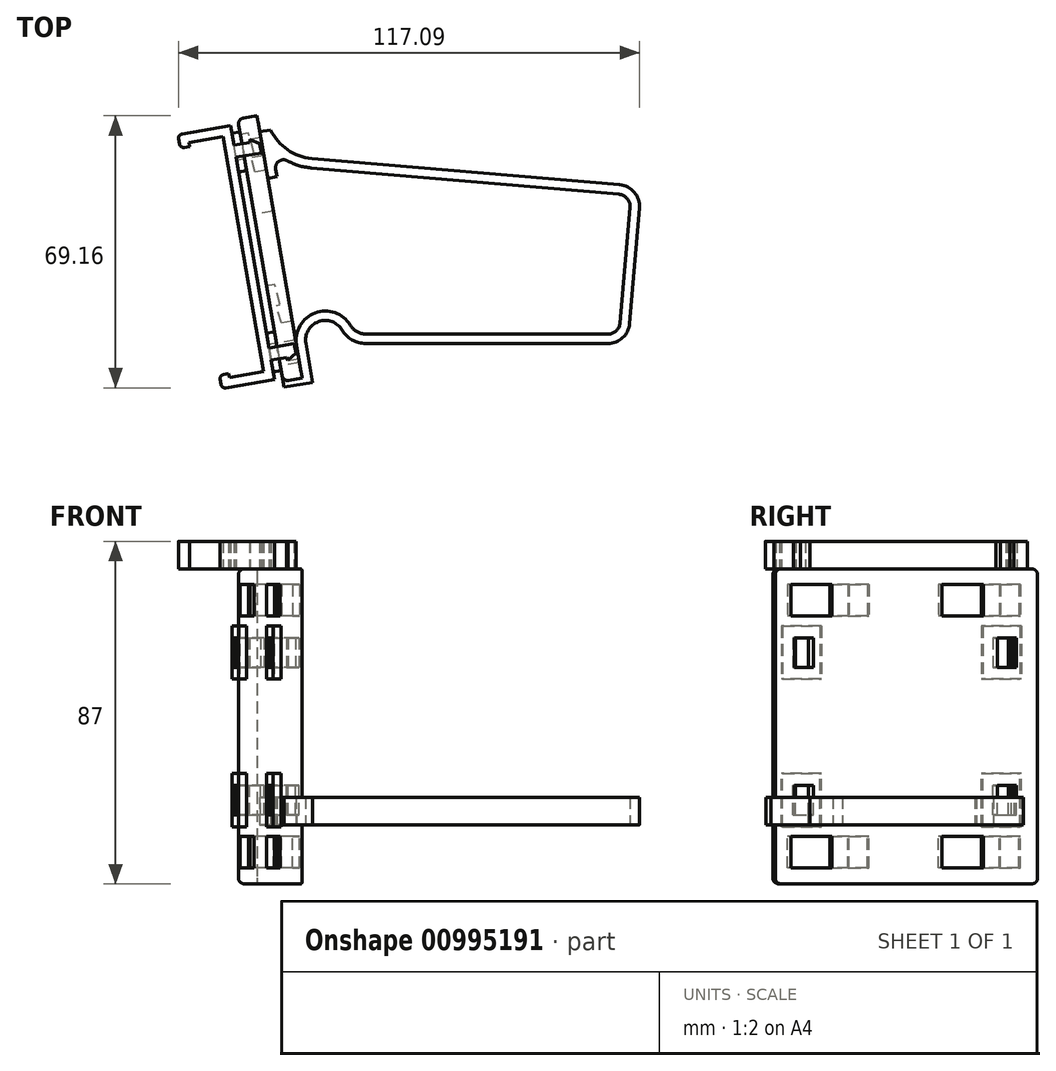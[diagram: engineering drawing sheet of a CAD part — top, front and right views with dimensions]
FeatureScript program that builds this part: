
annotation { "Feature Type Name" : "Feature", "Feature Type Description" : "" }
export const myFeature = defineFeature(function(context is Context, id is Id, definition is map)
    precondition{}
    {
        {
            var Q0;
            Q0=qCreatedBy(makeId("Top.planeOp"),FACE);
            var sketch = newSketch(context, id + "F0", { "sketchPlane" : qUnion([Q0])});
            skLineSegment(sketch, "E0", {"start": v(-25.97, -73.08) * mm, "end": v(35.99, -73.08) * mm});
            skLineSegment(sketch, "E1", {"start": v(41.47, -68) * mm, "end": v(43.72, -38.68) * mm});
            skLineSegment(sketch, "E2", {"start": v(38.66, -32.78) * mm, "end": v(-48.59, -26.08) * mm});
            skArc(sketch, "E3", {"start": v(-48.59, -26.08) * mm, "mid": v(-53.42, -24.82) * mm, "end": v(-57.51, -21.94) * mm});
            skLineSegment(sketch, "E4", {"start": v(-30.72, -73.08) * mm, "end": v(-30.72, -93.16) * mm, "construction": true});
            skArc(sketch, "E5", {"start": v(-31.66, -70.17) * mm, "mid": v(-37.97, -68.62) * mm, "end": v(-40.48, -74.62) * mm});
            skLineSegment(sketch, "E6", {"start": v(-57.51, -21.94) * mm, "end": v(-40.48, -74.62) * mm, "construction": true});
            skPoint(sketch, "E7.orphan", {"position": v(-40.72, -73.08) * mm});
            skLineSegment(sketch, "E8", {"start": v(-40.48, -74.62) * mm, "end": v(-37.4, -84.14) * mm});
            skPoint(sketch, "E9.visualSharp", {"position": v(-30.72, -73.08) * mm});
            skArc(sketch, "E9.filletArc", {"start": v(-31.66, -70.17) * mm, "mid": v(-29.17, -72.31) * mm, "end": v(-25.97, -73.08) * mm});
            skPoint(sketch, "E10.visualSharp", {"position": v(41.08, -73.08) * mm});
            skArc(sketch, "E10.filletArc", {"start": v(35.99, -73.08) * mm, "mid": v(39.72, -71.62) * mm, "end": v(41.47, -68) * mm});
            skPoint(sketch, "E11.visualSharp", {"position": v(44.14, -33.2) * mm});
            skArc(sketch, "E11.filletArc", {"start": v(43.72, -38.68) * mm, "mid": v(42.41, -34.68) * mm, "end": v(38.66, -32.78) * mm});
            skArc(sketch, "E12.0", {"start": v(-29.7, -68.77) * mm, "mid": v(-39.06, -66.48) * mm, "end": v(-42.76, -75.36) * mm});
            skArc(sketch, "E12.1", {"start": v(-29.7, -68.77) * mm, "mid": v(-28.07, -70.18) * mm, "end": v(-25.97, -70.68) * mm});
            skLineSegment(sketch, "E12.2", {"start": v(-25.97, -70.68) * mm, "end": v(35.99, -70.68) * mm});
            skArc(sketch, "E12.3", {"start": v(35.99, -70.68) * mm, "mid": v(38.1, -69.86) * mm, "end": v(39.08, -67.82) * mm});
            skArc(sketch, "E12.4", {"start": v(-48.77, -28.48) * mm, "mid": v(-58.05, -24.7) * mm, "end": v(-63.43, -16.25) * mm});
            skLineSegment(sketch, "E12.5", {"start": v(38.47, -35.17) * mm, "end": v(-48.77, -28.48) * mm});
            skArc(sketch, "E12.6", {"start": v(41.33, -38.5) * mm, "mid": v(40.59, -36.24) * mm, "end": v(38.47, -35.17) * mm});
            skLineSegment(sketch, "E12.7", {"start": v(39.08, -67.82) * mm, "end": v(41.33, -38.5) * mm});
            skLineSegment(sketch, "E13", {"start": v(-57.51, -21.94) * mm, "end": v(-63.43, -16.25) * mm});
            skLineSegment(sketch, "E14", {"start": v(-37.4, -84.14) * mm, "end": v(-44.25, -86.35) * mm});
            skLineSegment(sketch, "E15", {"start": v(-44.25, -86.35) * mm, "end": v(-47.94, -74.93) * mm});
            skLineSegment(sketch, "E16", {"start": v(-47.94, -74.93) * mm, "end": v(-46.04, -74.32) * mm});
            skLineSegment(sketch, "E17", {"start": v(-46.04, -74.32) * mm, "end": v(-43.94, -78.86) * mm});
            skLineSegment(sketch, "E18", {"start": v(-43.94, -78.86) * mm, "end": v(-44.5, -79.1) * mm});
            skLineSegment(sketch, "E19", {"start": v(-44.5, -79.1) * mm, "end": v(-42.4, -83.65) * mm});
            skLineSegment(sketch, "E20", {"start": v(-42.4, -83.65) * mm, "end": v(-40.3, -82.97) * mm});
            skLineSegment(sketch, "E21", {"start": v(-40.3, -82.97) * mm, "end": v(-46, -65.34) * mm});
            skLineSegment(sketch, "E22.0", {"start": v(-39.68, -84.87) * mm, "end": v(-37.4, -84.14) * mm, "construction": true});
            skLineSegment(sketch, "E22.1", {"start": v(-39.68, -84.87) * mm, "end": v(-40.3, -82.97) * mm, "construction": true});
            skLineSegment(sketch, "E22.9", {"start": v(-44.5, -79.1) * mm, "end": v(-46.04, -74.32) * mm, "construction": true});
            skLineSegment(sketch, "E23", {"start": v(15.23, 0) * mm, "end": v(76.75, 0) * mm});
            skLineSegment(sketch, "E24", {"start": v(82.23, 5.03) * mm, "end": v(84.73, 34.37) * mm});
            skLineSegment(sketch, "E25", {"start": v(79.72, 40.32) * mm, "end": v(1.5, 47) * mm});
            skArc(sketch, "E26", {"start": v(1.5, 47) * mm, "mid": v(-4.68, 49.24) * mm, "end": v(-8.92, 54.27) * mm});
            skLineSegment(sketch, "E27", {"start": v(0, 0) * mm, "end": v(-9.93, 57.5) * mm, "construction": true});
            skArc(sketch, "E28", {"start": v(0, 0) * mm, "mid": v(3.2, 5.54) * mm, "end": v(9.22, 3.41) * mm});
            skArc(sketch, "E29.filletArc", {"start": v(9.22, 3.41) * mm, "mid": v(11.78, 0.91) * mm, "end": v(15.23, 0) * mm});
            skPoint(sketch, "E30.visualSharp", {"position": v(81.8, 0) * mm});
            skArc(sketch, "E30.filletArc", {"start": v(76.75, 0) * mm, "mid": v(80.47, 1.45) * mm, "end": v(82.23, 5.03) * mm});
            skPoint(sketch, "E31.visualSharp", {"position": v(85.2, 39.86) * mm});
            skArc(sketch, "E31.filletArc", {"start": v(84.73, 34.37) * mm, "mid": v(83.46, 38.39) * mm, "end": v(79.72, 40.32) * mm});
            skArc(sketch, "E32.0", {"start": v(1.3, 44.6) * mm, "mid": v(-1.8, 45.2) * mm, "end": v(-4.72, 46.44) * mm});
            skLineSegment(sketch, "E32.1", {"start": v(79.52, 37.93) * mm, "end": v(1.3, 44.6) * mm});
            skArc(sketch, "E32.2", {"start": v(82.34, 34.58) * mm, "mid": v(81.63, 36.84) * mm, "end": v(79.52, 37.93) * mm});
            skLineSegment(sketch, "E32.3", {"start": v(79.84, 5.24) * mm, "end": v(82.34, 34.58) * mm});
            skArc(sketch, "E32.4", {"start": v(-2.36, -0.4) * mm, "mid": v(2.36, 7.8) * mm, "end": v(11.28, 4.64) * mm});
            skArc(sketch, "E32.5", {"start": v(11.28, 4.64) * mm, "mid": v(12.96, 3) * mm, "end": v(15.23, 2.4) * mm});
            skLineSegment(sketch, "E32.6", {"start": v(15.23, 2.4) * mm, "end": v(76.75, 2.4) * mm});
            skArc(sketch, "E32.7", {"start": v(76.75, 2.4) * mm, "mid": v(78.85, 3.22) * mm, "end": v(79.84, 5.24) * mm});
            skLineSegment(sketch, "E33", {"start": v(0, 0) * mm, "end": v(1.7, -9.85) * mm});
            skLineSegment(sketch, "E34", {"start": v(1.7, -9.85) * mm, "end": v(-5.59, -11.11) * mm});
            skLineSegment(sketch, "E35", {"start": v(-5.59, -11.11) * mm, "end": v(-7.63, 0.71) * mm});
            skLineSegment(sketch, "E36", {"start": v(-7.63, 0.71) * mm, "end": v(-5.66, 1.05) * mm});
            skLineSegment(sketch, "E37", {"start": v(-2.36, -0.4) * mm, "end": v(-1, -8.3) * mm});
            skLineSegment(sketch, "E38", {"start": v(-1, -8.3) * mm, "end": v(-3.96, -8.8) * mm});
            skLineSegment(sketch, "E39", {"start": v(-5.66, 1.05) * mm, "end": v(-3.96, -8.8) * mm, "construction": true});
            skPoint(sketch, "E40", {"position": v(-4.81, -3.88) * mm});
            skLineSegment(sketch, "E41", {"start": v(-5.3, -4) * mm, "end": v(-4.33, -3.74) * mm});
            skLineSegment(sketch, "E42", {"start": v(-5.66, 1.05) * mm, "end": v(-4.33, -3.74) * mm});
            skLineSegment(sketch, "E43", {"start": v(-5.3, -4) * mm, "end": v(-3.96, -8.8) * mm});
            skLineSegment(sketch, "E44", {"start": v(-7.66, 44.35) * mm, "end": v(-7.32, 42.37) * mm});
            skLineSegment(sketch, "E45", {"start": v(-7.32, 42.37) * mm, "end": v(-14.61, 41.11) * mm});
            skLineSegment(sketch, "E46", {"start": v(-14.61, 41.11) * mm, "end": v(-16.65, 52.94) * mm});
            skLineSegment(sketch, "E47", {"start": v(-16.65, 52.94) * mm, "end": v(-14.68, 53.28) * mm});
            skLineSegment(sketch, "E48", {"start": v(-11.73, 53.79) * mm, "end": v(-10.02, 43.93) * mm});
            skLineSegment(sketch, "E49", {"start": v(-10.02, 43.93) * mm, "end": v(-12.98, 43.42) * mm});
            skLineSegment(sketch, "E50", {"start": v(-14.68, 53.28) * mm, "end": v(-12.98, 43.42) * mm, "construction": true});
            skPoint(sketch, "E51", {"position": v(-13.83, 48.35) * mm});
            skLineSegment(sketch, "E52", {"start": v(-14.31, 48.22) * mm, "end": v(-13.35, 48.48) * mm});
            skLineSegment(sketch, "E53", {"start": v(-14.68, 53.28) * mm, "end": v(-13.35, 48.48) * mm});
            skLineSegment(sketch, "E54", {"start": v(-14.31, 48.22) * mm, "end": v(-12.98, 43.42) * mm});
            skLineSegment(sketch, "E55", {"start": v(-8.92, 54.27) * mm, "end": v(-9.36, 54.2) * mm, "construction": true});
            skPoint(sketch, "E56", {"position": v(-9.02, 52.22) * mm});
            skArc(sketch, "E57.filletArc", {"start": v(-4.72, 46.44) * mm, "mid": v(-6.85, 46.32) * mm, "end": v(-7.66, 44.35) * mm});
            skLineSegment(sketch, "E58", {"start": v(-8.92, 54.27) * mm, "end": v(-11.73, 53.79) * mm});
            skSolve(sketch);
        }
        {
            var Q0;
            Q0=makeQuery(id+"F0.imprint","IMPRINT",FACE,{"disambiguationData":[TD([[makeQuery(id+"F0.imprint","IMPRINT",EDGE,{"derivedFrom":sQuery(id+"F0.wireOp",EDGE,"E23")}),1.0]])]});
            extrude(context, id + "F1", {"entities" : qUnion([Q0]), "depth" : 7 * mm, "offsetDistance" : 25 * mm});
        }
        {
            var Q0;
            Q0=qCreatedBy(makeId("Top.planeOp"),FACE);
            cPlane(context, id + "F2", {"entities" : qUnion([Q0]), "cplaneType" : CPlaneType.OFFSET, "offset" : 25 * mm, "width" : 150 * mm, "height" : 150 * mm});
        }
        {
            var Q0;
            Q0=qCreatedBy(id+"F2.planeOp",FACE);
            var sketch = newSketch(context, id + "F3", { "sketchPlane" : qUnion([Q0])});
            skLineSegment(sketch, "E59.0.9", {"start": v(-3.39, 5.5) * mm, "end": v(-6.34, 5) * mm});
            skLineSegment(sketch, "E59.0.10", {"start": v(-6.34, 5) * mm, "end": v(-7.68, 9.78) * mm});
            skLineSegment(sketch, "E59.0.11", {"start": v(-7.68, 9.78) * mm, "end": v(-6.71, 10.05) * mm});
            skLineSegment(sketch, "E59.0.12", {"start": v(-6.71, 10.05) * mm, "end": v(-8.04, 14.85) * mm});
            skLineSegment(sketch, "E59.0.13", {"start": v(-8.04, 14.85) * mm, "end": v(-10.02, 14.5) * mm});
            skLineSegment(sketch, "E59.0.27", {"start": v(-10.02, 43.93) * mm, "end": v(-12.98, 43.42) * mm});
            skLineSegment(sketch, "E59.0.28", {"start": v(-12.98, 43.42) * mm, "end": v(-14.31, 48.22) * mm});
            skLineSegment(sketch, "E59.0.29", {"start": v(-14.31, 48.22) * mm, "end": v(-13.35, 48.48) * mm});
            skLineSegment(sketch, "E59.0.30", {"start": v(-13.35, 48.48) * mm, "end": v(-14.68, 53.28) * mm});
            skLineSegment(sketch, "E59.0.31", {"start": v(-14.68, 53.28) * mm, "end": v(-16.65, 52.94) * mm});
            skLineSegment(sketch, "E60", {"start": v(-3.39, 5.5) * mm, "end": v(-1.6, -4.84) * mm});
            skLineSegment(sketch, "E61", {"start": v(-1.6, -4.84) * mm, "end": v(-6.53, -5.7) * mm});
            skLineSegment(sketch, "E62", {"start": v(-10.02, 14.5) * mm, "end": v(-6.53, -5.7) * mm});
            skLineSegment(sketch, "E63.0", {"start": v(-7.94, 15.02) * mm, "end": v(-10.04, 14.65) * mm});
            skLineSegment(sketch, "E63.1", {"start": v(-3.41, 5.65) * mm, "end": v(-6.23, 5.16) * mm});
            skLineSegment(sketch, "E63.2", {"start": v(-6.23, 5.16) * mm, "end": v(-7.5, 9.68) * mm});
            skLineSegment(sketch, "E63.3", {"start": v(-7.5, 9.68) * mm, "end": v(-6.53, 9.95) * mm});
            skLineSegment(sketch, "E63.4", {"start": v(-6.53, 9.95) * mm, "end": v(-7.94, 15.02) * mm});
            skLineSegment(sketch, "E64", {"start": v(-10.02, 43.93) * mm, "end": v(-8.24, 33.59) * mm});
            skLineSegment(sketch, "E65", {"start": v(-8.24, 33.59) * mm, "end": v(-13.16, 32.74) * mm});
            skLineSegment(sketch, "E66", {"start": v(-16.65, 52.94) * mm, "end": v(-13.16, 32.74) * mm});
            skLineSegment(sketch, "E67.0", {"start": v(-14.57, 53.45) * mm, "end": v(-16.68, 53.08) * mm});
            skLineSegment(sketch, "E67.1", {"start": v(-10.05, 44.08) * mm, "end": v(-12.87, 43.6) * mm});
            skLineSegment(sketch, "E67.2", {"start": v(-12.87, 43.6) * mm, "end": v(-14.13, 48.11) * mm});
            skLineSegment(sketch, "E67.3", {"start": v(-14.13, 48.11) * mm, "end": v(-13.17, 48.38) * mm});
            skLineSegment(sketch, "E67.4", {"start": v(-13.17, 48.38) * mm, "end": v(-14.57, 53.45) * mm});
            skLineSegment(sketch, "E68", {"start": v(-10.05, 44.08) * mm, "end": v(-10.02, 43.93) * mm});
            skLineSegment(sketch, "E69", {"start": v(-16.68, 53.08) * mm, "end": v(-16.65, 52.94) * mm});
            skLineSegment(sketch, "E70", {"start": v(-3.41, 5.65) * mm, "end": v(-3.39, 5.5) * mm});
            skLineSegment(sketch, "E71", {"start": v(-10.04, 14.65) * mm, "end": v(-10.02, 14.5) * mm});
            skLineSegment(sketch, "E72", {"start": v(-12.43, 57.88) * mm, "end": v(-17.36, 57.03) * mm});
            skLineSegment(sketch, "E73", {"start": v(-17.36, 57.03) * mm, "end": v(-5.84, -9.64) * mm});
            skLineSegment(sketch, "E74", {"start": v(-5.84, -9.64) * mm, "end": v(-0.92, -8.79) * mm});
            skLineSegment(sketch, "E75", {"start": v(-0.92, -8.79) * mm, "end": v(-12.43, 57.88) * mm});
            skLineSegment(sketch, "E76.0", {"start": v(-1.6, -4.84) * mm, "end": v(-6.53, -5.7) * mm, "construction": true});
            skSolve(sketch);
        }
        {
            var Q0;
            Q0 = qSketchRegion(id + "F3", true);
            extrude(context, id + "F4", {"entities" : qUnion([Q0]), "endBound" : BoundingType.SYMMETRIC, "depth" : 80 * mm, "offsetDistance" : 25 * mm});
        }
        {
            var Q0;
            {var subQ0=sQuery(id+"F3.wireOp",EDGE,"E59.0.9");Q0=makeQuery(id+"F3.imprint","IMPRINT",FACE,{"disambiguationData":[TD([[makeQuery(id+"F3.imprint","IMPRINT",EDGE,{"derivedFrom":subQ0}),1.0]])]});}
            var Q1;
            {var subQ3=sQuery(id+"F3.wireOp",EDGE,"E59.0.9");Q1=makeQuery(id+"F3.imprint","IMPRINT",FACE,{"disambiguationData":[TD([[makeQuery(id+"F3.imprint","IMPRINT",EDGE,{"derivedFrom":subQ3}),-1.0]])]});}
            var Q2;
            {var subQ0=sQuery(id+"F3.wireOp",EDGE,"E59.0.27");Q2=makeQuery(id+"F3.imprint","IMPRINT",FACE,{"disambiguationData":[TD([[makeQuery(id+"F3.imprint","IMPRINT",EDGE,{"derivedFrom":subQ0}),1.0]])]});}
            var Q3;
            {var subQ1=sQuery(id+"F3.wireOp",EDGE,"E59.0.27");Q3=makeQuery(id+"F3.imprint","IMPRINT",FACE,{"disambiguationData":[TD([[makeQuery(id+"F3.imprint","IMPRINT",EDGE,{"derivedFrom":subQ1}),-1.0]])]});}
            extrude(context, id + "F5", {"entities" : qUnion([Q0, Q1, Q2, Q3]), "operationType" : NewBodyOperationType.REMOVE, "depth" : 36 * mm, "offsetDistance" : 25 * mm, "hasSecondDirection" : true, "secondDirectionOppositeDirection" : false, "secondDirectionDepth" : 28 * mm});
        }
        {
            var Q0;
            {var subQ0=sQuery(id+"F3.wireOp",EDGE,"E59.0.9");Q0=makeQuery(id+"F3.imprint","IMPRINT",FACE,{"disambiguationData":[TD([[makeQuery(id+"F3.imprint","IMPRINT",EDGE,{"derivedFrom":subQ0}),1.0]])]});}
            var Q1;
            {var subQ3=sQuery(id+"F3.wireOp",EDGE,"E59.0.9");Q1=makeQuery(id+"F3.imprint","IMPRINT",FACE,{"disambiguationData":[TD([[makeQuery(id+"F3.imprint","IMPRINT",EDGE,{"derivedFrom":subQ3}),-1.0]])]});}
            var Q2;
            {var subQ0=sQuery(id+"F3.wireOp",EDGE,"E59.0.27");Q2=makeQuery(id+"F3.imprint","IMPRINT",FACE,{"disambiguationData":[TD([[makeQuery(id+"F3.imprint","IMPRINT",EDGE,{"derivedFrom":subQ0}),1.0]])]});}
            var Q3;
            {var subQ1=sQuery(id+"F3.wireOp",EDGE,"E59.0.27");Q3=makeQuery(id+"F3.imprint","IMPRINT",FACE,{"disambiguationData":[TD([[makeQuery(id+"F3.imprint","IMPRINT",EDGE,{"derivedFrom":subQ1}),-1.0]])]});}
            extrude(context, id + "F6", {"entities" : qUnion([Q0, Q1, Q2, Q3]), "operationType" : NewBodyOperationType.REMOVE, "oppositeDirection" : true, "depth" : 36 * mm, "offsetDistance" : 25 * mm, "hasSecondDirection" : true, "secondDirectionOppositeDirection" : true, "secondDirectionDepth" : 28 * mm});
        }
        {
            var Q0;
            Q0=makeQuery(id+"F4.opExtrude","CAP_FACE",FACE,{"disambiguationData":[OSD([sQuery(id+"F3.wireOp",EDGE,"E72"),sQuery(id+"F3.wireOp",EDGE,"E73"),sQuery(id+"F3.wireOp",EDGE,"E74"),sQuery(id+"F3.wireOp",EDGE,"E75")])],"isStart":false});
            var sketch = newSketch(context, id + "F7", { "sketchPlane" : qUnion([Q0])});
            skLineSegment(sketch, "E77", {"start": v(-7.96, -9.12) * mm, "end": v(-19.1, 55.32) * mm});
            skLineSegment(sketch, "E78", {"start": v(-19.1, 55.32) * mm, "end": v(-32.5, 53) * mm});
            skLineSegment(sketch, "E79", {"start": v(-32.5, 53) * mm, "end": v(-31.92, 49.66) * mm});
            skLineSegment(sketch, "E80", {"start": v(-31.92, 49.66) * mm, "end": v(-29.55, 50.07) * mm});
            skLineSegment(sketch, "E81", {"start": v(-29.55, 50.07) * mm, "end": v(-29.72, 51.05) * mm});
            skLineSegment(sketch, "E82", {"start": v(-29.72, 51.05) * mm, "end": v(-21.05, 52.55) * mm});
            skLineSegment(sketch, "E83", {"start": v(-21.05, 52.55) * mm, "end": v(-10.74, -7.17) * mm});
            skLineSegment(sketch, "E84", {"start": v(-10.74, -7.17) * mm, "end": v(-19.4, -8.66) * mm});
            skLineSegment(sketch, "E85", {"start": v(-19.4, -8.66) * mm, "end": v(-19.58, -7.68) * mm});
            skLineSegment(sketch, "E86", {"start": v(-19.58, -7.68) * mm, "end": v(-21.94, -8.09) * mm});
            skLineSegment(sketch, "E87", {"start": v(-21.94, -8.09) * mm, "end": v(-21.36, -11.44) * mm});
            skLineSegment(sketch, "E88", {"start": v(-21.36, -11.44) * mm, "end": v(-7.96, -9.12) * mm});
            skLineSegment(sketch, "E89", {"start": v(-8.81, -4.2) * mm, "end": v(-4.87, -3.51) * mm});
            skLineSegment(sketch, "E90", {"start": v(-4.87, -3.51) * mm, "end": v(-4.48, -4.2) * mm});
            skLineSegment(sketch, "E91", {"start": v(-4.48, -4.2) * mm, "end": v(-2.53, -2.36) * mm});
            skLineSegment(sketch, "E92", {"start": v(-2.53, -2.36) * mm, "end": v(-2.94, 0) * mm});
            skLineSegment(sketch, "E93", {"start": v(-2.94, 0) * mm, "end": v(-9.35, -1.1) * mm});
            skLineSegment(sketch, "E94", {"start": v(-13.53, 23.1) * mm, "end": v(-15.9, 22.7) * mm, "construction": true});
            skLineSegment(sketch, "E95.MirrorCS", {"start": v(-14.3, 51.08) * mm, "end": v(-14.16, 51.86) * mm});
            skLineSegment(sketch, "E96.MirrorCS", {"start": v(-18.24, 50.4) * mm, "end": v(-14.3, 51.08) * mm});
            skLineSegment(sketch, "E97.MirrorCS", {"start": v(-11.3, 48.41) * mm, "end": v(-17.71, 47.3) * mm});
            skLineSegment(sketch, "E98.MirrorCS", {"start": v(-11.71, 50.78) * mm, "end": v(-11.3, 48.41) * mm});
            skLineSegment(sketch, "E99.MirrorCS", {"start": v(-14.16, 51.86) * mm, "end": v(-11.71, 50.78) * mm});
            skLineSegment(sketch, "E100.0", {"start": v(-17.36, 57.03) * mm, "end": v(-5.84, -9.64) * mm});
            skSolve(sketch);
        }
        {
            var Q0;
            {var subQ6=sQuery(id+"F7.wireOp",EDGE,"E79");Q0=makeQuery(id+"F7.imprint","IMPRINT",FACE,{"disambiguationData":[TD([[makeQuery(id+"F7.imprint","IMPRINT",EDGE,{"derivedFrom":subQ6}),1.0]])]});}
            var Q1;
            {var subQ0=sQuery(id+"F7.wireOp",EDGE,"E77");var subQ6=sQuery(id+"F7.wireOp",EDGE,"E88");var subQ10=makeQuery(id+"F7.imprint","INTERSECT",VERTEX,{"derivedFrom":[subQ0,subQ6]});Q1=makeQuery(id+"F7.imprint","IMPRINT",FACE,{"disambiguationData":[TD([[makeQuery(id+"F7.imprint","IMPRINT",EDGE,{"disambiguationData":[TD([[subQ10,-1.0]])],"derivedFrom":subQ0}),1.0]])]});}
            var Q2;
            {var subQ1=sQuery(id+"F7.wireOp",EDGE,"E95.MirrorCS");Q2=makeQuery(id+"F7.imprint","IMPRINT",FACE,{"disambiguationData":[TD([[makeQuery(id+"F7.imprint","IMPRINT",EDGE,{"derivedFrom":subQ1}),-1.0]])]});}
            var Q3;
            {var subQ0=sQuery(id+"F7.wireOp",EDGE,"E98.MirrorCS");Q3=makeQuery(id+"F7.imprint","IMPRINT",FACE,{"disambiguationData":[TD([[makeQuery(id+"F7.imprint","IMPRINT",EDGE,{"derivedFrom":subQ0}),-1.0]])]});}
            var Q4;
            {var subQ0=sQuery(id+"F7.wireOp",EDGE,"E92");Q4=makeQuery(id+"F7.imprint","IMPRINT",FACE,{"disambiguationData":[TD([[makeQuery(id+"F7.imprint","IMPRINT",EDGE,{"derivedFrom":subQ0}),1.0]])]});}
            var Q5;
            {var subQ4=sQuery(id+"F7.wireOp",EDGE,"E89");Q5=makeQuery(id+"F7.imprint","IMPRINT",FACE,{"disambiguationData":[TD([[makeQuery(id+"F7.imprint","IMPRINT",EDGE,{"derivedFrom":subQ4}),1.0]])]});}
            var Q6;
            {var subQ0=sQuery(id+"F7.wireOp",EDGE,"E96.MirrorCS");var subQ1=sQuery(id+"F7.wireOp",EDGE,"E77");var subQ2=makeQuery(id+"F7.imprint","INTERSECT",VERTEX,{"derivedFrom":[subQ1,subQ0]});Q6=makeQuery(id+"F7.imprint","IMPRINT",FACE,{"disambiguationData":[TD([[makeQuery(id+"F7.imprint","IMPRINT",EDGE,{"disambiguationData":[TD([[subQ2,1.0]])],"derivedFrom":subQ1}),-1.0]])]});}
            extrude(context, id + "F8", {"entities" : qUnion([Q0, Q1, Q2, Q3, Q4, Q5, Q6]), "depth" : 7 * mm, "offsetDistance" : 25 * mm});
        }
        {
            var Q0;
            Q0=makeQuery(id+"F8.opExtrude","SWEPT_EDGE",EDGE,{"disambiguationData":[OSD([sQuery(id+"F7.wireOp",EDGE,"E87"),sQuery(id+"F7.wireOp",EDGE,"E88")])]});
            var Q1;
            Q1=makeQuery(id+"F8.opExtrude","SWEPT_EDGE",EDGE,{"disambiguationData":[OSD([sQuery(id+"F7.wireOp",EDGE,"E86"),sQuery(id+"F7.wireOp",EDGE,"E87")])]});
            var Q2;
            Q2=makeQuery(id+"F8.opExtrude","SWEPT_EDGE",EDGE,{"disambiguationData":[OSD([sQuery(id+"F7.wireOp",EDGE,"E78"),sQuery(id+"F7.wireOp",EDGE,"E79")])]});
            var Q3;
            Q3=makeQuery(id+"F8.opExtrude","SWEPT_EDGE",EDGE,{"disambiguationData":[OSD([sQuery(id+"F7.wireOp",EDGE,"E79"),sQuery(id+"F7.wireOp",EDGE,"E80")])]});
            fillet(context, id + "F9", {"entities" : qUnion([Q0, Q1, Q2, Q3]), "radius" : 1 * mm, "tangentPropagation" : true, "allowEdgeOverflow" : false});
        }
        {
            var Q0;
            Q0=makeQuery(id+"F4.opExtrude","SWEPT_EDGE",EDGE,{"disambiguationData":[OSD([sQuery(id+"F3.wireOp",EDGE,"E72"),sQuery(id+"F3.wireOp",EDGE,"E73")])]});
            cPoint(context, id + "F10", {"entities" : qUnion([Q0]), "parameter" : 0.5});
        }
        {
            var Q0;
            {var subQ10=sQuery(id+"F7.wireOp",EDGE,"E90");Q0=makeQuery(id+"F7.imprint","IMPRINT",FACE,{"disambiguationData":[TD([[makeQuery(id+"F7.imprint","IMPRINT",EDGE,{"derivedFrom":subQ10}),-1.0]])]});}
            var Q1;
            Q1 = qCreatedBy(id + "F10" ,VERTEX);
            cPlane(context, id + "F11", {"entities" : qUnion([Q0, Q1]), "cplaneType" : CPlaneType.PLANE_POINT, "offset" : 25 * mm, "width" : 150 * mm, "height" : 150 * mm});
        }
        {
            var Q0;
            Q0=qCreatedBy(id+"F11.planeOp",FACE);
            var sketch = newSketch(context, id + "F12", { "sketchPlane" : qUnion([Q0])});
            skLineSegment(sketch, "E101.0", {"start": v(-10.81, 48.5) * mm, "end": v(-17.71, 47.3) * mm, "construction": true});
            skLineSegment(sketch, "E101.1", {"start": v(-2.45, 0.09) * mm, "end": v(-9.35, -1.1) * mm, "construction": true});
            skLineSegment(sketch, "E102.0", {"start": v(-14.3, 51.08) * mm, "end": v(-14.16, 51.86) * mm, "construction": true});
            skLineSegment(sketch, "E103.0", {"start": v(-18.24, 50.4) * mm, "end": v(-14.3, 51.08) * mm, "construction": true});
            skLineSegment(sketch, "E104.0", {"start": v(-8.81, -4.2) * mm, "end": v(-4.87, -3.51) * mm, "construction": true});
            skLineSegment(sketch, "E105.0", {"start": v(-4.87, -3.51) * mm, "end": v(-4.48, -4.2) * mm, "construction": true});
            skLineSegment(sketch, "E106.0", {"start": v(-0.92, -8.79) * mm, "end": v(-12.43, 57.88) * mm, "construction": true});
            skPoint(sketch, "E107.orphan", {"position": v(-2.94, 0) * mm});
            skPoint(sketch, "E108.orphan", {"position": v(-11.3, 48.41) * mm});
            skLineSegment(sketch, "E109.0", {"start": v(-2.59, 0.87) * mm, "end": v(-9.48, -0.32) * mm});
            skLineSegment(sketch, "E110.0", {"start": v(-10.68, 47.71) * mm, "end": v(-17.57, 46.52) * mm});
            skLineSegment(sketch, "E111", {"start": v(-4.48, -4.2) * mm, "end": v(-1.79, -3.74) * mm, "construction": true});
            skLineSegment(sketch, "E112.0", {"start": v(-4.53, -4.32) * mm, "end": v(-1.77, -3.84) * mm});
            skLineSegment(sketch, "E112.1", {"start": v(-4.92, -3.62) * mm, "end": v(-4.53, -4.32) * mm});
            skLineSegment(sketch, "E112.2", {"start": v(-8.8, -4.3) * mm, "end": v(-4.92, -3.62) * mm});
            skLineSegment(sketch, "E113", {"start": v(-14.16, 51.86) * mm, "end": v(-11.47, 52.33) * mm, "construction": true});
            skLineSegment(sketch, "E114.0", {"start": v(-14.25, 51.95) * mm, "end": v(-11.5, 52.43) * mm});
            skLineSegment(sketch, "E114.1", {"start": v(-14.39, 51.16) * mm, "end": v(-14.25, 51.95) * mm});
            skLineSegment(sketch, "E114.2", {"start": v(-18.26, 50.5) * mm, "end": v(-14.39, 51.16) * mm});
            skLineSegment(sketch, "E115", {"start": v(-8.8, -4.3) * mm, "end": v(-9.48, -0.32) * mm});
            skLineSegment(sketch, "E116", {"start": v(-1.77, -3.84) * mm, "end": v(-2.59, 0.87) * mm});
            skLineSegment(sketch, "E117", {"start": v(-17.57, 46.52) * mm, "end": v(-18.26, 50.5) * mm});
            skLineSegment(sketch, "E118", {"start": v(-10.68, 47.71) * mm, "end": v(-11.5, 52.43) * mm});
            skLineSegment(sketch, "E119", {"start": v(-9.48, -0.32) * mm, "end": v(-17.57, 46.52) * mm, "construction": true});
            skLineSegment(sketch, "E120", {"start": v(-13.53, 23.1) * mm, "end": v(-6.63, 24.3) * mm, "construction": true});
            skSolve(sketch);
        }
        {
            var Q0;
            Q0=makeQuery(id+"F12.imprint","IMPRINT",FACE,{"disambiguationData":[TD([[makeQuery(id+"F12.imprint","IMPRINT",EDGE,{"derivedFrom":sQuery(id+"F12.wireOp",EDGE,"E109.0")}),1.0]])]});
            var sketch = newSketch(context, id + "F13", { "sketchPlane" : qUnion([Q0])});
            skLineSegment(sketch, "E121", {"start": v(-6.32, -6.9) * mm, "end": v(-8.02, 2.96) * mm});
            skLineSegment(sketch, "E122", {"start": v(-8.02, 2.96) * mm, "end": v(-10, 2.62) * mm});
            skLineSegment(sketch, "E123", {"start": v(-10, 2.62) * mm, "end": v(-8.29, -7.23) * mm});
            skLineSegment(sketch, "E124", {"start": v(-6.32, -6.9) * mm, "end": v(-8.29, -7.23) * mm});
            skLineSegment(sketch, "E125.0", {"start": v(-13.53, 23.1) * mm, "end": v(-6.63, 24.3) * mm, "construction": true});
            skLineSegment(sketch, "E126.MirrorCS", {"start": v(-16.8, 53.77) * mm, "end": v(-18.77, 53.43) * mm});
            skLineSegment(sketch, "E127.MirrorCS", {"start": v(-16.8, 53.77) * mm, "end": v(-15.1, 43.92) * mm});
            skLineSegment(sketch, "E128.MirrorCS", {"start": v(-15.1, 43.92) * mm, "end": v(-17.07, 43.58) * mm});
            skLineSegment(sketch, "E129.MirrorCS", {"start": v(-17.07, 43.58) * mm, "end": v(-18.77, 53.43) * mm});
            skSolve(sketch);
        }
        {
            var Q0;
            Q0 = qSketchRegion(id + "F13", true);
            extrude(context, id + "F14", {"entities" : qUnion([Q0]), "operationType" : NewBodyOperationType.ADD, "oppositeDirection" : true, "depth" : 25.5 * mm, "offsetDistance" : 25 * mm, "hasSecondDirection" : true, "secondDirectionOppositeDirection" : true, "secondDirectionDepth" : 12 * mm});
        }
        {
            var Q0;
            Q0 = qSketchRegion(id + "F13", true);
            extrude(context, id + "F15", {"entities" : qUnion([Q0]), "operationType" : NewBodyOperationType.ADD, "depth" : 25.5 * mm, "offsetDistance" : 25 * mm, "hasSecondDirection" : true, "secondDirectionOppositeDirection" : false, "secondDirectionDepth" : 12 * mm});
        }
        {
            var Q0;
            Q0 = qSketchRegion(id + "F12", true);
            extrude(context, id + "F16", {"entities" : qUnion([Q0]), "operationType" : NewBodyOperationType.REMOVE, "oppositeDirection" : true, "depth" : 22.5 * mm, "offsetDistance" : 25 * mm, "hasSecondDirection" : true, "secondDirectionOppositeDirection" : true, "secondDirectionDepth" : 15 * mm});
        }
        {
            var Q0;
            Q0 = qSketchRegion(id + "F12", true);
            extrude(context, id + "F17", {"entities" : qUnion([Q0]), "operationType" : NewBodyOperationType.REMOVE, "depth" : 22.5 * mm, "offsetDistance" : 25 * mm, "hasSecondDirection" : true, "secondDirectionOppositeDirection" : false, "secondDirectionDepth" : 15 * mm});
        }
        {
            var Q0;
            Q0=makeQuery(id+"F4.opExtrude","CAP_EDGE",EDGE,{"disambiguationData":[OSD([sQuery(id+"F3.wireOp",EDGE,"E74")])],"isStart":true});
            var Q1;
            Q1=makeQuery(id+"F4.opExtrude","CAP_EDGE",EDGE,{"disambiguationData":[OSD([sQuery(id+"F3.wireOp",EDGE,"E74")])],"isStart":false});
            var Q2;
            Q2=makeQuery(id+"F4.opExtrude","CAP_EDGE",EDGE,{"disambiguationData":[OSD([sQuery(id+"F3.wireOp",EDGE,"E72")])],"isStart":false});
            var Q3;
            Q3=makeQuery(id+"F4.opExtrude","CAP_EDGE",EDGE,{"disambiguationData":[OSD([sQuery(id+"F3.wireOp",EDGE,"E72")])],"isStart":true});
            fillet(context, id + "F18", {"entities" : qUnion([Q0, Q1, Q2, Q3]), "radius" : 1.5 * mm, "tangentPropagation" : true, "allowEdgeOverflow" : false});
        }
        {
            var Q0;
            Q0=makeQuery(id+"F4.opExtrude","CAP_EDGE",EDGE,{"disambiguationData":[OSD([sQuery(id+"F3.wireOp",EDGE,"E73")])],"isStart":true});
            fillet(context, id + "F19", {"entities" : qUnion([Q0]), "radius" : 1.5 * mm, "tangentPropagation" : true, "allowEdgeOverflow" : false});
        }
    });
